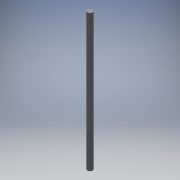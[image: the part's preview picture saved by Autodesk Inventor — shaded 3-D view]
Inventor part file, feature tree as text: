
AUTODESK INVENTOR PART (.ipt)
format: ipt  version: 2016 (Build 200138000, 138)  size: 90,112 bytes
history: native  units: mm
features: extrude x1, thread x1, sketch x1
ambient origin geometry x8: Origin, YZ Plane, XZ Plane, XY Plane, X Axis, Y Axis, Z Axis, Center Point
bodies: Solid1 (feature_tree)
feature tree (3):
  extrude  "Extrusion1"  Depth=210.0mm TaperAngle=0.0deg
  thread  "Thread1"  [1 undecoded]
  sketch  "Sketch1"  dims[d0=8.0mm d1=210.0mm d2=0.0mm d3=10.0mm d4=0.0mm]
note: 1 required parameter value undecoded (feature->parameter linkage not recoverable at this tier; creation-order binding heuristic only, values carry confidence <= 0.55)
